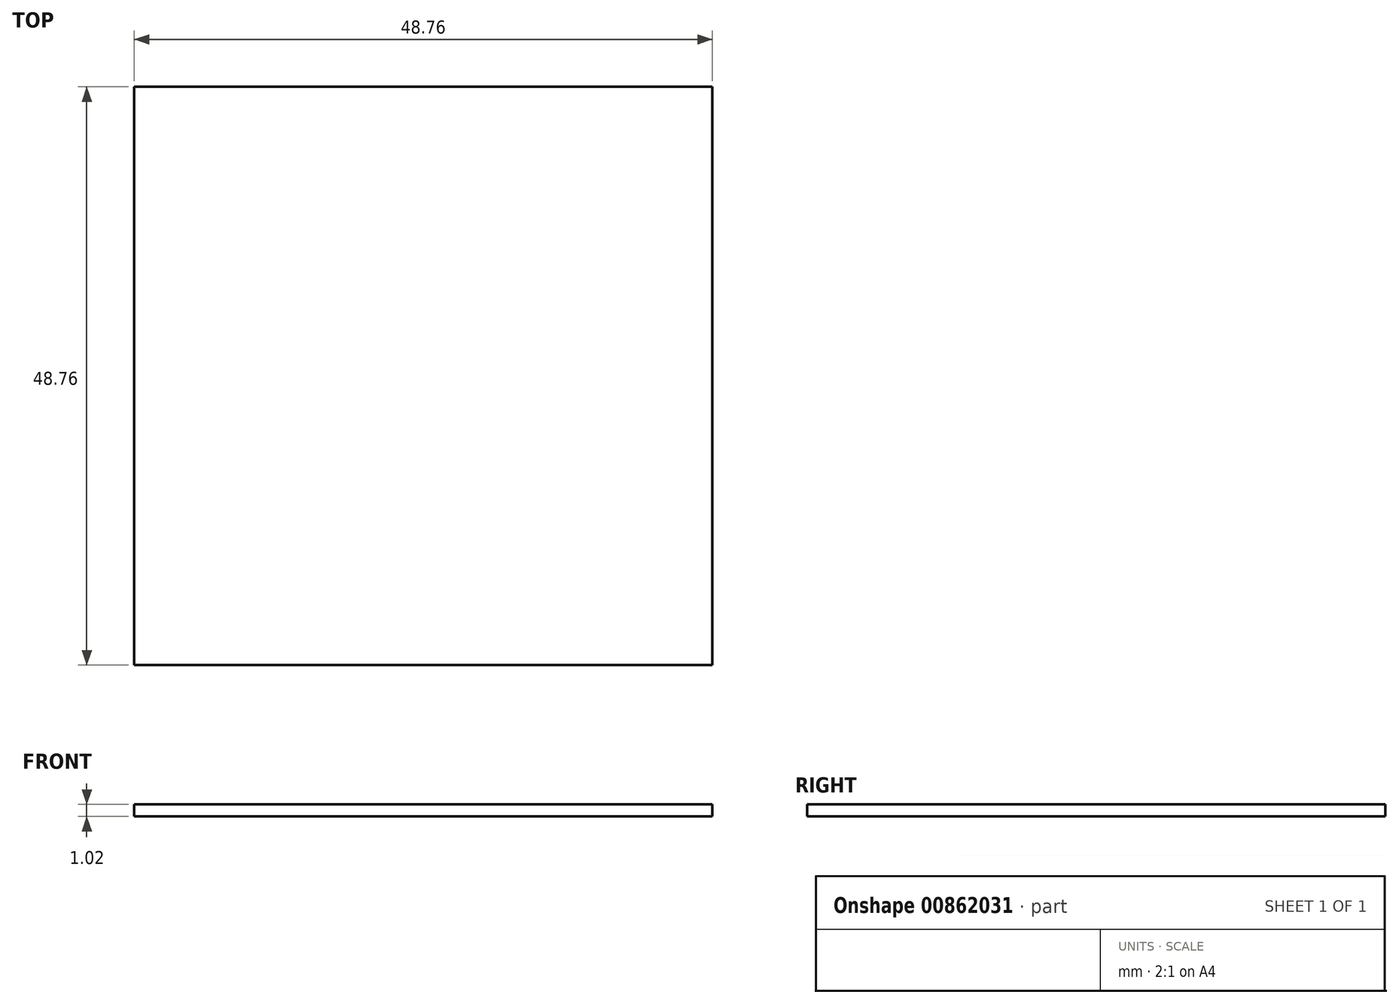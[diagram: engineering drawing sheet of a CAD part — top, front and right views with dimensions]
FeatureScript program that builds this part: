
annotation { "Feature Type Name" : "Feature", "Feature Type Description" : "" }
export const myFeature = defineFeature(function(context is Context, id is Id, definition is map)
    precondition{}
    {
        {
            var Q0;
            Q0=qCreatedBy(makeId("Top.planeOp"),FACE);
            var sketch = newSketch(context, id + "F0", { "sketchPlane" : qUnion([Q0])});
            skLineSegment(sketch, "E0.bottom", {"start": v(0, 0) * mm, "end": v(50.8, 0) * mm});
            skLineSegment(sketch, "E0.top", {"start": v(0, 50.8) * mm, "end": v(50.8, 50.8) * mm});
            skLineSegment(sketch, "E0.left", {"start": v(0, 0) * mm, "end": v(0, 50.8) * mm});
            skLineSegment(sketch, "E0.right", {"start": v(50.8, 0) * mm, "end": v(50.8, 50.8) * mm});
            skSolve(sketch);
        }
        {
            var Q0;
            Q0=makeQuery(id+"F0.imprint","IMPRINT",FACE,{"disambiguationData":[TD([[makeQuery(id+"F0.imprint","IMPRINT",EDGE,{"derivedFrom":sQuery(id+"F0.wireOp",EDGE,"E0.bottom")}),1.0]])]});
            var sketch = newSketch(context, id + "F1", { "sketchPlane" : qUnion([Q0])});
            skLineSegment(sketch, "E1.0", {"start": v(1.02, 49.78) * mm, "end": v(49.78, 49.78) * mm});
            skLineSegment(sketch, "E1.1", {"start": v(1.02, 1.02) * mm, "end": v(1.02, 49.78) * mm});
            skLineSegment(sketch, "E1.2", {"start": v(1.02, 1.02) * mm, "end": v(49.78, 1.02) * mm});
            skLineSegment(sketch, "E1.3", {"start": v(49.78, 1.02) * mm, "end": v(49.78, 49.78) * mm});
            skSolve(sketch);
        }
        {
            var Q0;
            Q0=makeQuery(id+"F1.imprint","IMPRINT",FACE,{"disambiguationData":[TD([[makeQuery(id+"F1.imprint","IMPRINT",EDGE,{"derivedFrom":sQuery(id+"F1.wireOp",EDGE,"E1.0")}),-1.0]])]});
            extrude(context, id + "F2", {"entities" : qUnion([Q0]), "depth" : 1.02 * mm, "offsetDistance" : 25 * mm});
        }
    });
